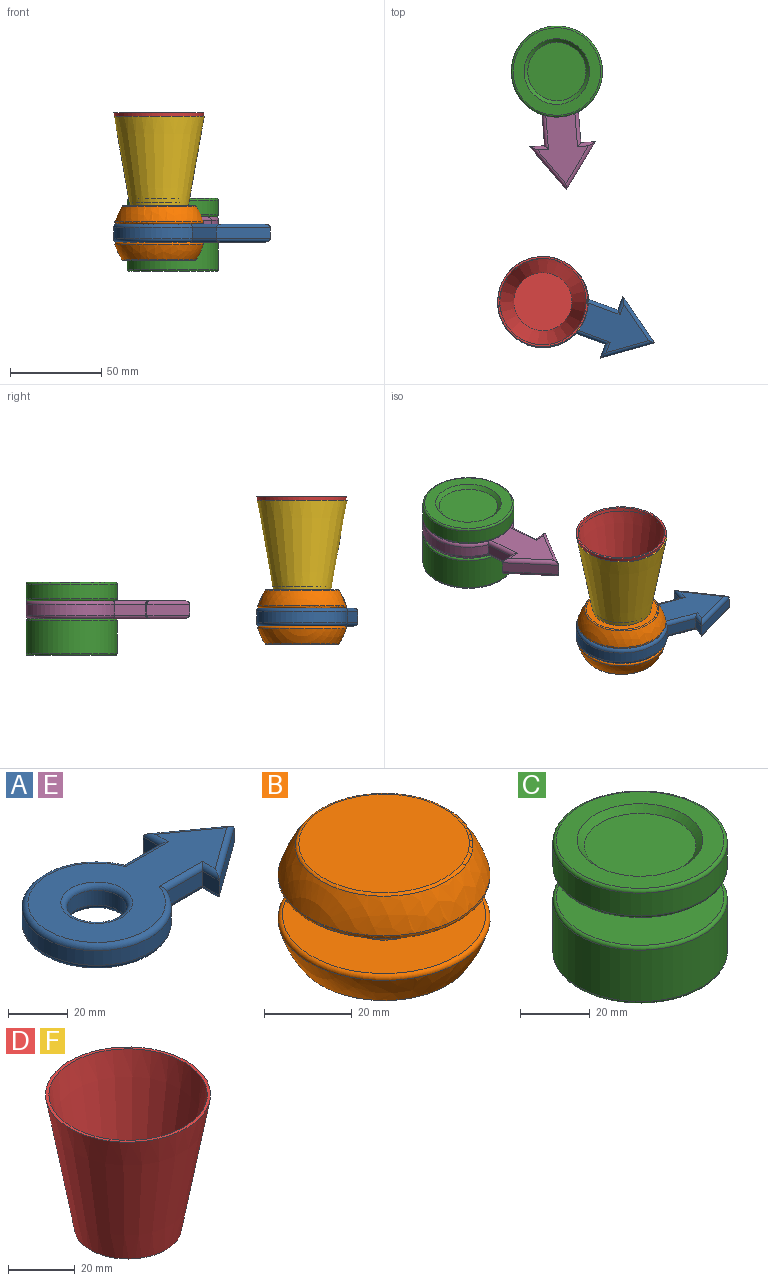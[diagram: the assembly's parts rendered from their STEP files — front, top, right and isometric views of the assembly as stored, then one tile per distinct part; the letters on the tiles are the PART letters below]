
ASSEMBLY  parts=6 mates=4
PART A: 26 faces, bbox 92.1x54.1x10 mm
  f0: plane 8x6mm, normal (-1,0,0), area 48mm2, adj f1,f6,f10,f18
  f1: plane 17.09x6mm, normal (0,1,0), area 102.5mm2, adj f0,f2,f11,f19
  f2: cylinder r=25mm len=50mm, axis (0,0,-1), area 819mm2, adj f1,f3,f13,f21
  f3: plane 17.09x6mm, normal (0,-1,0), area 102.5mm2, adj f2,f4,f15,f23
  f4: plane 8x6mm, normal (-1,0,0), area 48mm2, adj f3,f5,f16,f24
  f5: plane 25x18mm, normal (0.58,-0.81,0), area 184.8mm2, adj f4,f6,f14,f22
  f6: plane 25x18mm, normal (0.58,0.81,0), area 184.8mm2, adj f0,f5,f12,f20
  f7: cylinder r=10mm len=20mm, axis (0,0,-1), area 377mm2, adj f17,f25
  f8: plane 84.58x46mm, normal (0,0,1), area 1797mm2, adj f18,f19,f20,f21,f22,f23,f24,f25
  f9: plane 84.58x46mm, normal (0,0,-1), area 1797mm2, adj f10,f11,f12,f13,f14,f15,f16,f17
  f10: cylinder r=2mm len=10mm, axis (0,-1,0), area 23mm2, adj f0,f9,f11,f12
  f11: cylinder r=2mm len=20.44mm, axis (-1,0,0), area 57.5mm2, adj f1,f9,f10,f13
  f12: cylinder r=2mm len=26.17mm, axis (-0.81,0.58,0), area 89.2mm2, adj f6,f9,f10,f14
  f13: torus R=23mm, axis (0,0,1), area 419.3mm2, adj f2,f9,f11,f15
  f14: cylinder r=2mm len=26.17mm, axis (0.81,0.58,0), area 89.2mm2, adj f5,f9,f12,f16
  f15: cylinder r=2mm len=20.44mm, axis (1,0,0), area 57.5mm2, adj f3,f9,f13,f16
  f16: cylinder r=2mm len=10mm, axis (0,-1,0), area 23mm2, adj f4,f9,f14,f15
  f17: torus R=12mm, axis (0,0,1), area 211.7mm2, adj f7,f9
  f18: cylinder r=2mm len=10mm, axis (0,1,0), area 23mm2, adj f0,f8,f19,f20
  f19: cylinder r=2mm len=20.44mm, axis (1,0,0), area 57.5mm2, adj f1,f8,f18,f21
  f20: cylinder r=2mm len=26.17mm, axis (0.81,-0.58,0), area 89.2mm2, adj f6,f8,f18,f22
  f21: torus R=23mm, axis (0,0,1), area 419.3mm2, adj f2,f8,f19,f23
  f22: cylinder r=2mm len=26.17mm, axis (-0.81,-0.58,0), area 89.2mm2, adj f5,f8,f20,f24
  f23: cylinder r=2mm len=20.44mm, axis (-1,0,0), area 57.5mm2, adj f3,f8,f21,f24
  f24: cylinder r=2mm len=10mm, axis (0,1,0), area 23mm2, adj f4,f8,f22,f23
  f25: torus R=12mm, axis (0,0,1), area 211.7mm2, adj f7,f8
PART B: 11 faces, bbox 52.5x52.5x50 mm
  f0: sphere r=25mm, area 1308.7mm2, adj f7,f9
  f1: plane 46.48x46.48mm, normal (0,0,1), area 1382.3mm2, adj f6,f9
  f2: plane 38.99x38.99mm, normal (0,0,-1), area 1193.8mm2, adj f7
  f3: sphere r=25mm, area 1309mm2, adj f8,f10
  f4: plane 46.48x46.48mm, normal (0,0,-1), area 1382.3mm2, adj f6,f10
  f5: plane 38.99x38.99mm, normal (0,0,1), area 1193.8mm2, adj f8
  f6: cylinder r=10mm len=20mm, axis (0,0,-1), area 628.3mm2, adj f1,f4
  f7: torus R=19.49mm, axis (0,0,1), area 118.7mm2, adj f0,f2
  f8: torus R=19.49mm, axis (0,0,1), area 118.7mm2, adj f3,f5
  f9: torus R=23.24mm, axis (0,0,1), area 274.1mm2, adj f0,f1
  f10: torus R=23.24mm, axis (0,0,1), area 274.1mm2, adj f3,f4
PART C: 13 faces, bbox 54.1x54.1x40 mm
  f0: cylinder r=25mm len=50mm, axis (0,0,-1), area 2827.4mm2, adj f9,f10
  f1: plane 48x48mm, normal (0,0,1), area 1495.4mm2, adj f3,f10
  f2: plane 48x48mm, normal (0,0,-1), area 1809.6mm2, adj f9
  f3: cylinder r=10mm len=20mm, axis (0,0,-1), area 628.3mm2, adj f1,f6
  f4: cylinder r=25mm len=50mm, axis (0,0,-1), area 1256.6mm2, adj f7,f8
  f5: plane 48x48mm, normal (0,0,1), area 791.7mm2, adj f8,f12
  f6: plane 48x48mm, normal (0,0,-1), area 1495.4mm2, adj f3,f7
  f7: torus R=24mm, axis (0,0,1), area 243.2mm2, adj f4,f6
  f8: torus R=24mm, axis (0,0,1), area 243.2mm2, adj f4,f5
  f9: torus R=24mm, axis (0,0,1), area 243.2mm2, adj f0,f2
  f10: torus R=24mm, axis (0,0,1), area 243.2mm2, adj f0,f1
  f11: plane 32x32mm, normal (0,0,1), area 804.2mm2, adj f12
  f12: cone r=16mm half-angle=45deg, axis (0,0,1), area 302.1mm2, adj f5,f11
PART D: 5 faces, bbox 49.5x49.5x49 mm
  f0: plane 32x32mm, normal (0,0,1), area 804.2mm2, adj f4
  f1: plane 32x32mm, normal (0,0,-1), area 804.2mm2, adj f2
  f2: cone r=16mm half-angle=10.1deg, axis (0,0,1), area 6372.4mm2, adj f1,f3
  f3: plane 49.47x49.47mm, normal (0,0,1), area 152.3mm2, adj f2,f4
  f4: cone r=23.73mm half-angle=9.7deg, axis (0,0,1), area 5702.6mm2, adj f0,f3
PART E: same geometry as A
PART F: same geometry as D
PLACE A rot(axis=(0,0,-1),20.1deg) t=(-4.93,18.06,0.39)mm
PLACE B t=(-4.93,18.06,5.39)mm fixed
PLACE C t=(2.58,144.53,-15.56)mm fixed
PLACE D t=(-5.07,18.25,25.48)mm
PLACE E rot(axis=(0,0,-1),85.4deg) t=(2.58,144.53,4.44)mm
PLACE F t=(-4.93,18.06,23.43)mm
MATE planar C.f12 <-> D.f2  axis (0,0,1) through (2.58,144.53,22.44)mm
MATE fastened F.f2 <-> B.f8  axis (0,0,-1) through (-4.93,18.06,20.39)mm
MATE revolute B.f7 <-> A.f7  axis (0,0,-1) through (-4.93,18.06,10.39)mm
MATE revolute C.f0 <-> E.f7  axis (0,0,1) through (2.58,144.53,4.44)mm
